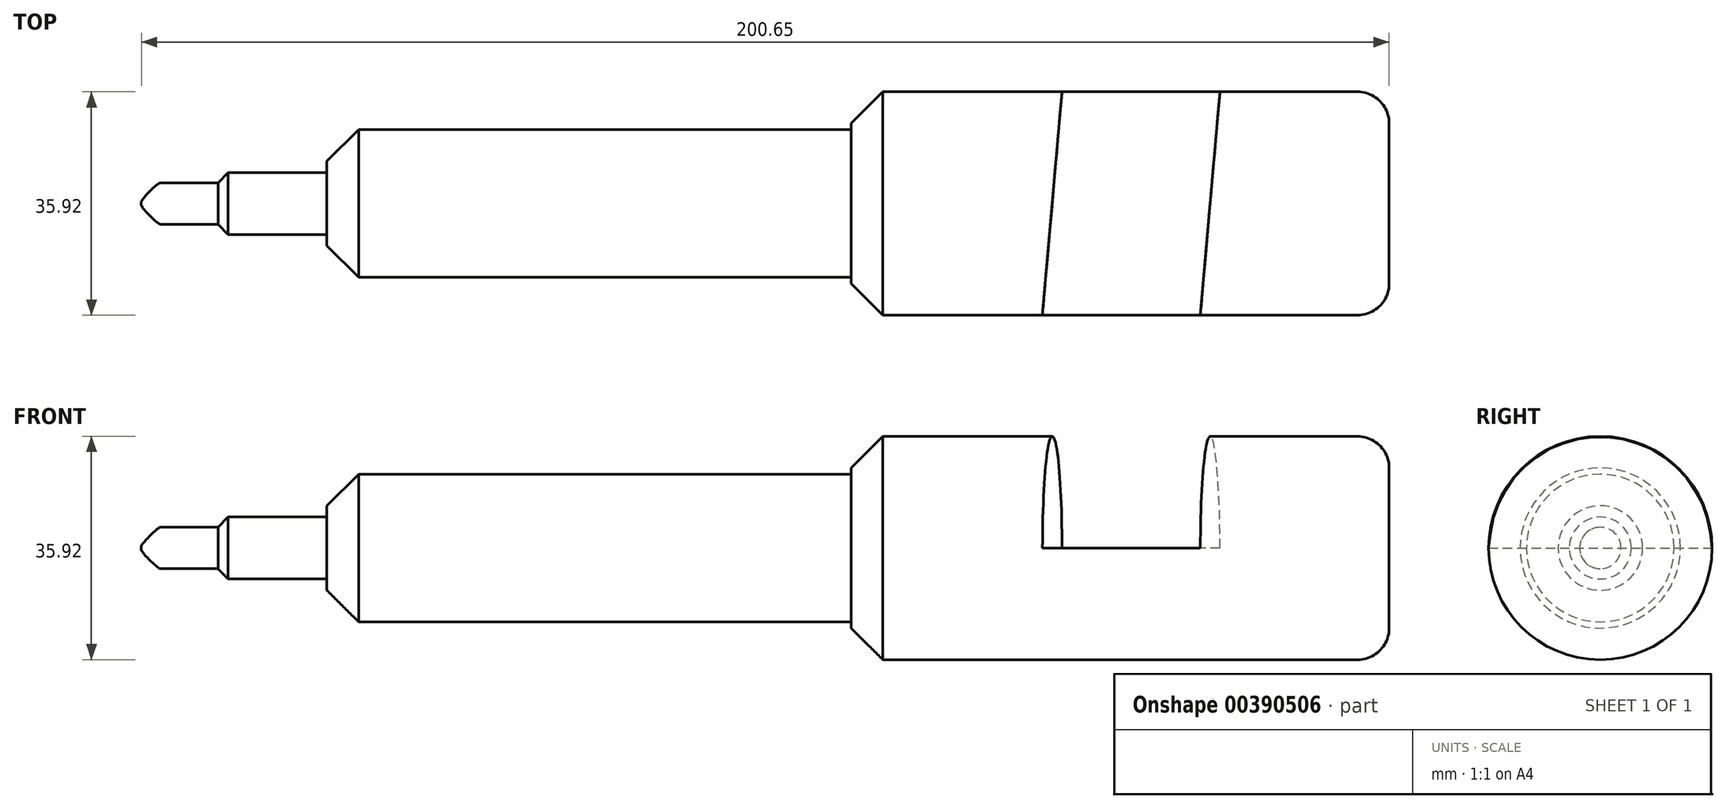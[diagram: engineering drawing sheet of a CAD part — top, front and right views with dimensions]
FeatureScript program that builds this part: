
annotation { "Feature Type Name" : "Feature", "Feature Type Description" : "" }
export const myFeature = defineFeature(function(context is Context, id is Id, definition is map)
    precondition{}
    {
        {
            var Q0;
            Q0=qCreatedBy(makeId("Right.planeOp"),FACE);
            var sketch = newSketch(context, id + "F0", { "sketchPlane" : qUnion([Q0])});
            skCircle(sketch, "E0", {"center": v(0, 0) * mm, "radius": 17.96 * mm});
            skSolve(sketch);
        }
        {
            var Q0;
            Q0=makeQuery(id+"F0.imprint","IMPRINT",FACE,{"disambiguationData":[TD([[makeQuery(id+"F0.imprint","IMPRINT",EDGE,{"derivedFrom":sQuery(id+"F0.wireOp",EDGE,"E0")}),1.0]])]});
            var sketch = newSketch(context, id + "F1", { "sketchPlane" : qUnion([Q0])});
            skSolve(sketch);
        }
        {
            var Q0;
            Q0=makeQuery(id+"F1.imprint","IMPRINT",FACE,{"disambiguationData":[TD([[makeQuery(id+"F1.imprint","IMPRINT",EDGE,{"derivedFrom":makeQuery(id+"F0.imprint","IMPRINT",EDGE,{"derivedFrom":sQuery(id+"F0.wireOp",EDGE,"E0")})}),1.0]])]});
            extrude(context, id + "F2", {"entities" : qUnion([Q0]), "depth" : 86.5 * mm});
        }
        {
            var Q0;
            Q0=qCreatedBy(makeId("Right.planeOp"),FACE);
            var sketch = newSketch(context, id + "F3", { "sketchPlane" : qUnion([Q0])});
            skCircle(sketch, "E1", {"center": v(0, 0) * mm, "radius": 11.87 * mm});
            skCircle(sketch, "E2", {"center": v(0, 0) * mm, "radius": 4.98 * mm});
            skSolve(sketch);
        }
        {
            var Q0;
            Q0 = qSketchRegion(id + "F3", true);
            extrude(context, id + "F4", {"entities" : qUnion([Q0]), "operationType" : NewBodyOperationType.ADD, "oppositeDirection" : true, "depth" : 84.3 * mm});
        }
        {
            var Q0;
            Q0=makeQuery(id+"F3.imprint","IMPRINT",FACE,{"disambiguationData":[TD([[makeQuery(id+"F3.imprint","IMPRINT",EDGE,{"derivedFrom":sQuery(id+"F3.wireOp",EDGE,"E2")}),1.0]])]});
            extrude(context, id + "F5", {"entities" : qUnion([Q0]), "operationType" : NewBodyOperationType.ADD, "oppositeDirection" : true, "depth" : 103.98 * mm});
        }
        {
            var Q0;
            Q0=makeQuery(id+"F2.opExtrude","CAP_EDGE",EDGE,{"disambiguationData":[OSD([sQuery(id+"F0.wireOp",EDGE,"E0")])],"isStart":false});
            fillet(context, id + "F6", {"entities" : qUnion([Q0]), "radius" : 5.08 * mm, "tangentPropagation" : true, "allowEdgeOverflow" : false});
        }
        {
            var Q0;
            Q0=makeQuery(id+"F2.opExtrude","CAP_EDGE",EDGE,{"disambiguationData":[OSD([sQuery(id+"F0.wireOp",EDGE,"E0")])],"isStart":true});
            chamfer(context, id + "F7", {"entities" : qUnion([Q0]), "width" : 5.08 * mm, "tangentPropagation" : true});
        }
        {
            var Q0;
            Q0=makeQuery(id+"F4.opExtrude","CAP_EDGE",EDGE,{"disambiguationData":[OSD([sQuery(id+"F3.wireOp",EDGE,"E1")])],"isStart":false});
            chamfer(context, id + "F8", {"entities" : qUnion([Q0]), "width" : 5.08 * mm, "tangentPropagation" : true});
        }
        {
            var Q0;
            Q0=makeQuery(id+"F5.opExtrude","CAP_FACE",FACE,{"disambiguationData":[OSD([sQuery(id+"F3.wireOp",EDGE,"E2")])],"isStart":false});
            var sketch = newSketch(context, id + "F9", { "sketchPlane" : qUnion([Q0])});
            skCircle(sketch, "E3", {"center": v(0, 0) * mm, "radius": 3.34 * mm});
            skSolve(sketch);
        }
        {
            var Q0;
            Q0=makeQuery(id+"F9.imprint","IMPRINT",FACE,{"disambiguationData":[TD([[makeQuery(id+"F9.imprint","IMPRINT",EDGE,{"derivedFrom":sQuery(id+"F9.wireOp",EDGE,"E3")}),1.0]])]});
            extrude(context, id + "F10", {"entities" : qUnion([Q0]), "operationType" : NewBodyOperationType.ADD, "depth" : 10.16 * mm});
        }
        {
            var Q0;
            Q0=makeQuery(id+"F5.opExtrude","CAP_EDGE",EDGE,{"disambiguationData":[OSD([sQuery(id+"F3.wireOp",EDGE,"E2")])],"isStart":false});
            chamfer(context, id + "F11", {"entities" : qUnion([Q0]), "chamferType" : ChamferType.OFFSET_ANGLE, "width" : 3.8 * mm, "oppositeDirection" : false, "angle" : 45 * degree, "tangentPropagation" : true});
        }
        {
            var Q0;
            Q0=makeQuery(id+"F10.opExtrude","CAP_EDGE",EDGE,{"disambiguationData":[OSD([sQuery(id+"F9.wireOp",EDGE,"E3")])],"isStart":false});
            fillet(context, id + "F12", {"entities" : qUnion([Q0]), "radius" : 3.05 * mm, "tangentPropagation" : true, "rho" : 0.1, "crossSection" : FilletCrossSection.CONIC, "allowEdgeOverflow" : false});
        }
        {
            var Q0;
            Q0=qCreatedBy(makeId("Top.planeOp"),FACE);
            var sketch = newSketch(context, id + "F13", { "sketchPlane" : qUnion([Q0])});
            skLineSegment(sketch, "E4", {"start": v(30.2, -24.33) * mm, "end": v(35.15, 32.12) * mm});
            skLineSegment(sketch, "E5", {"start": v(35.15, 32.12) * mm, "end": v(60.55, 32.12) * mm});
            skLineSegment(sketch, "E6", {"start": v(60.55, 32.12) * mm, "end": v(55.62, -24.16) * mm});
            skLineSegment(sketch, "E7", {"start": v(55.62, -24.16) * mm, "end": v(30.2, -24.33) * mm});
            skSolve(sketch);
        }
        {
            var Q0;
            Q0=makeQuery(id+"F13.imprint","IMPRINT",FACE,{"disambiguationData":[TD([[makeQuery(id+"F13.imprint","IMPRINT",EDGE,{"derivedFrom":sQuery(id+"F13.wireOp",EDGE,"E4")}),-1.0]])]});
            extrude(context, id + "F14", {"entities" : qUnion([Q0]), "operationType" : NewBodyOperationType.REMOVE, "depth" : 50.8 * mm});
        }
    });
